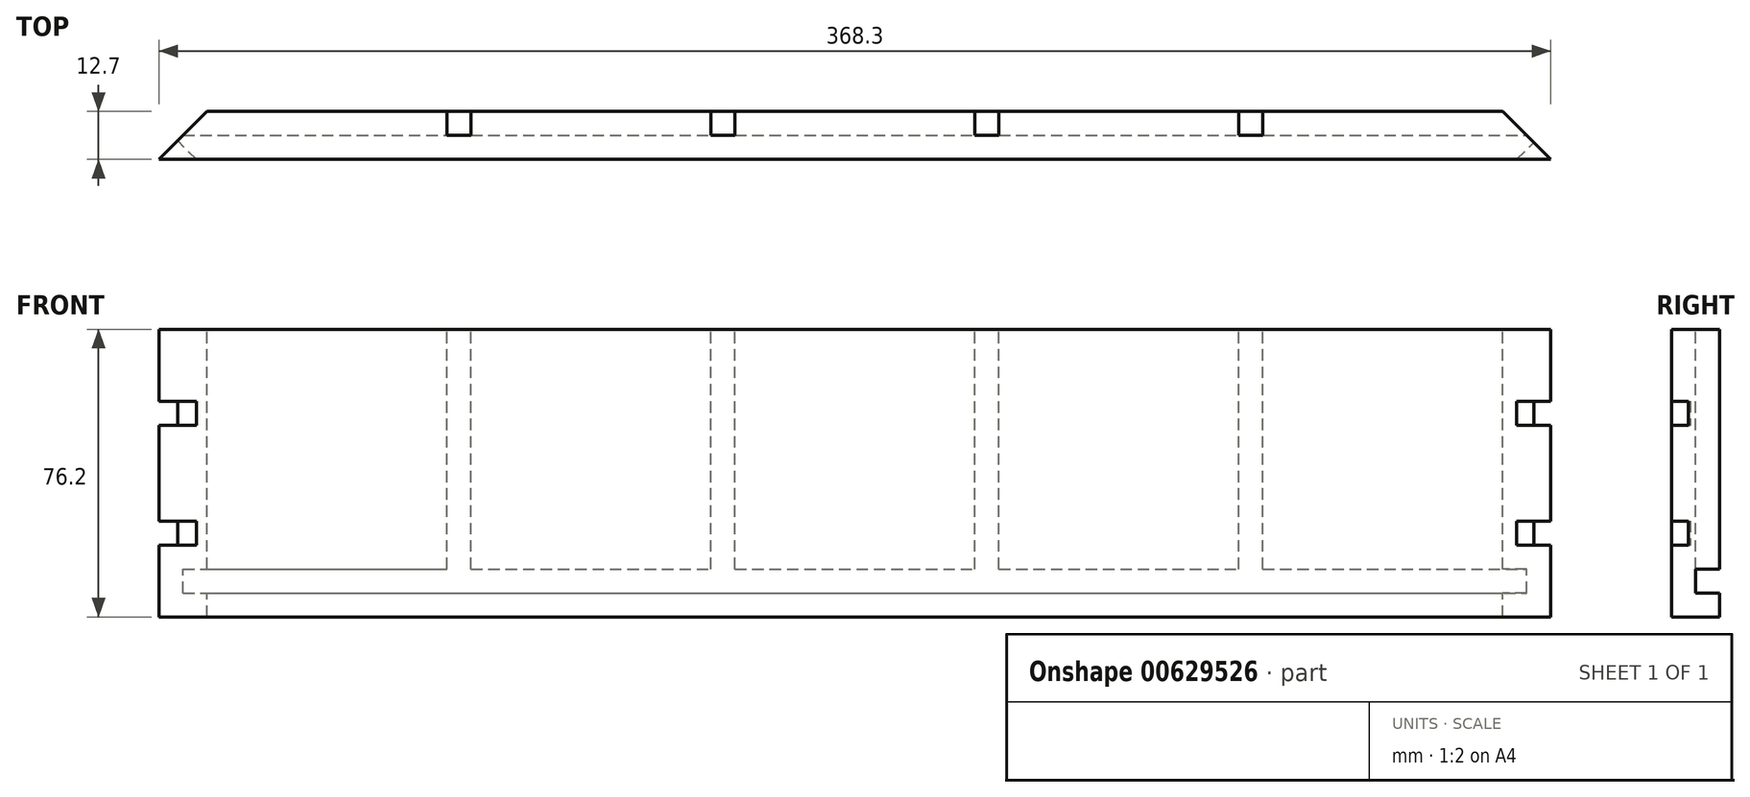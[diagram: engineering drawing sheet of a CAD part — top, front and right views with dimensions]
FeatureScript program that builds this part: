
annotation { "Feature Type Name" : "Feature", "Feature Type Description" : "" }
export const myFeature = defineFeature(function(context is Context, id is Id, definition is map)
    precondition{}
    {
        {
            var Q0;
            Q0=qCreatedBy(makeId("Front.planeOp"),FACE);
            var sketch = newSketch(context, id + "F0", { "sketchPlane" : qUnion([Q0])});
            skLineSegment(sketch, "E0.bottom", {"start": v(-184.15, 0) * mm, "end": v(184.15, 0) * mm});
            skLineSegment(sketch, "E0.top", {"start": v(-184.15, 76.2) * mm, "end": v(184.15, 76.2) * mm});
            skLineSegment(sketch, "E0.left", {"start": v(-184.15, 0) * mm, "end": v(-184.15, 76.2) * mm});
            skLineSegment(sketch, "E0.right", {"start": v(184.15, 0) * mm, "end": v(184.15, 76.2) * mm});
            skSolve(sketch);
        }
        {
            var Q0;
            Q0 = qSketchRegion(id + "F0", true);
            extrude(context, id + "F1", {"entities" : qUnion([Q0]), "depth" : 12.7 * mm, "offsetDistance" : 25.4 * mm});
        }
        {
            var Q0;
            Q0=makeQuery(id+"F1.opExtrude","SWEPT_FACE",FACE,{"disambiguationData":[OSD([sQuery(id+"F0.wireOp",EDGE,"E0.right")])]});
            var sketch = newSketch(context, id + "F2", { "sketchPlane" : qUnion([Q0])});
            skLineSegment(sketch, "E1.bottom", {"start": v(0, 12.7) * mm, "end": v(-6.35, 12.7) * mm});
            skLineSegment(sketch, "E1.top", {"start": v(0, 6.35) * mm, "end": v(-6.35, 6.35) * mm});
            skLineSegment(sketch, "E1.left", {"start": v(0, 12.7) * mm, "end": v(0, 6.35) * mm});
            skLineSegment(sketch, "E1.right", {"start": v(-6.35, 12.7) * mm, "end": v(-6.35, 6.35) * mm});
            skSolve(sketch);
        }
        {
            var Q0;
            Q0 = qSketchRegion(id + "F2", true);
            extrude(context, id + "F3", {"entities" : qUnion([Q0]), "operationType" : NewBodyOperationType.REMOVE, "endBound" : BoundingType.THROUGH_ALL, "oppositeDirection" : true, "depth" : 25.4 * mm, "offsetDistance" : 25.4 * mm});
        }
        {
            var Q0;
            Q0=makeQuery(id+"F1.opExtrude","SWEPT_FACE",FACE,{"disambiguationData":[OSD([sQuery(id+"F0.wireOp",EDGE,"E0.top")])]});
            var sketch = newSketch(context, id + "F4", { "sketchPlane" : qUnion([Q0])});
            skLineSegment(sketch, "E2", {"start": v(-184.15, -12.7) * mm, "end": v(-171.45, 0) * mm});
            skLineSegment(sketch, "E3", {"start": v(-171.45, 0) * mm, "end": v(-184.15, 0) * mm});
            skLineSegment(sketch, "E4", {"start": v(-184.15, 0) * mm, "end": v(-184.15, -12.7) * mm});
            skLineSegment(sketch, "E5.MirrorCS", {"start": v(184.15, 0) * mm, "end": v(184.15, -12.7) * mm});
            skLineSegment(sketch, "E6.MirrorCS", {"start": v(171.45, 0) * mm, "end": v(184.15, 0) * mm});
            skLineSegment(sketch, "E7.MirrorCS", {"start": v(184.15, -12.7) * mm, "end": v(171.45, 0) * mm});
            skSolve(sketch);
        }
        {
            var Q0;
            Q0 = qSketchRegion(id + "F4", true);
            extrude(context, id + "F5", {"entities" : qUnion([Q0]), "operationType" : NewBodyOperationType.REMOVE, "endBound" : BoundingType.THROUGH_ALL, "oppositeDirection" : true, "depth" : 25.4 * mm, "offsetDistance" : 25.4 * mm});
        }
        {
            var Q0;
            {var subQ0=sQuery(id+"F0.wireOp",EDGE,"E0.top");var subQ1=sQuery(id+"F0.wireOp",EDGE,"E0.left");var subQ2=sQuery(id+"F0.wireOp",EDGE,"E0.right");Q0=makeQuery(id+"F3.boolean.opBoolean","SPLIT",FACE,{"disambiguationData":[TD([makeQuery(id+"F1.opExtrude","SWEPT_FACE",FACE,{"disambiguationData":[OSD([subQ0])]})])],"derivedFrom":makeQuery(id+"F1.opExtrude","CAP_FACE",FACE,{"disambiguationData":[OSD([sQuery(id+"F0.wireOp",EDGE,"E0.bottom"),subQ0,subQ1,subQ2])],"isStart":true})});}
            var sketch = newSketch(context, id + "F6", { "sketchPlane" : qUnion([Q0])});
            skLineSegment(sketch, "E8.bottom", {"start": v(-107.95, 12.7) * mm, "end": v(-101.6, 12.7) * mm});
            skLineSegment(sketch, "E8.top", {"start": v(-107.95, 76.2) * mm, "end": v(-101.6, 76.2) * mm});
            skLineSegment(sketch, "E8.left", {"start": v(-101.6, 12.7) * mm, "end": v(-101.6, 76.2) * mm});
            skLineSegment(sketch, "E8.right", {"start": v(-107.95, 12.7) * mm, "end": v(-107.95, 76.2) * mm});
            skLineSegment(sketch, "E9.1.0.0", {"start": v(-38.1, 76.2) * mm, "end": v(-31.75, 76.2) * mm});
            skLineSegment(sketch, "E9.1.0.1", {"start": v(-31.75, 12.7) * mm, "end": v(-31.75, 76.2) * mm});
            skLineSegment(sketch, "E9.1.0.2", {"start": v(-38.1, 12.7) * mm, "end": v(-31.75, 12.7) * mm});
            skLineSegment(sketch, "E9.1.0.3", {"start": v(-38.1, 12.7) * mm, "end": v(-38.1, 76.2) * mm});
            skLineSegment(sketch, "E9.2.0.0", {"start": v(31.75, 76.2) * mm, "end": v(38.1, 76.2) * mm});
            skLineSegment(sketch, "E9.2.0.1", {"start": v(38.1, 12.7) * mm, "end": v(38.1, 76.2) * mm});
            skLineSegment(sketch, "E9.2.0.2", {"start": v(31.75, 12.7) * mm, "end": v(38.1, 12.7) * mm});
            skLineSegment(sketch, "E9.2.0.3", {"start": v(31.75, 12.7) * mm, "end": v(31.75, 76.2) * mm});
            skLineSegment(sketch, "E9.3.0.0", {"start": v(101.6, 76.2) * mm, "end": v(107.95, 76.2) * mm});
            skLineSegment(sketch, "E9.3.0.1", {"start": v(107.95, 12.7) * mm, "end": v(107.95, 76.2) * mm});
            skLineSegment(sketch, "E9.3.0.2", {"start": v(101.6, 12.7) * mm, "end": v(107.95, 12.7) * mm});
            skLineSegment(sketch, "E9.3.0.3", {"start": v(101.6, 12.7) * mm, "end": v(101.6, 76.2) * mm});
            skLineSegment(sketch, "E9.direction1", {"start": v(-107.95, 12.7) * mm, "end": v(-38.1, 12.7) * mm, "construction": true});
            skSolve(sketch);
        }
        {
            var Q0;
            Q0 = qSketchRegion(id + "F6", true);
            extrude(context, id + "F7", {"entities" : qUnion([Q0]), "operationType" : NewBodyOperationType.REMOVE, "oppositeDirection" : true, "depth" : 6.35 * mm, "offsetDistance" : 25.4 * mm});
        }
        {
            var Q0;
            Q0=makeQuery(id+"F5.boolean.opBoolean","COPY",FACE,{"derivedFrom":makeQuery(id+"F5.opExtrude","SWEPT_FACE",FACE,{"disambiguationData":[OSD([sQuery(id+"F4.wireOp",EDGE,"E2")])]})});
            var sketch = newSketch(context, id + "F8", { "sketchPlane" : qUnion([Q0])});
            skLineSegment(sketch, "E10.bottom", {"start": v(139.2, 57.15) * mm, "end": v(132.2, 57.15) * mm});
            skLineSegment(sketch, "E10.top", {"start": v(139.2, 50.8) * mm, "end": v(132.2, 50.8) * mm});
            skLineSegment(sketch, "E10.left", {"start": v(139.2, 57.15) * mm, "end": v(139.2, 50.8) * mm});
            skLineSegment(sketch, "E10.right", {"start": v(132.2, 57.15) * mm, "end": v(132.2, 50.8) * mm});
            skLineSegment(sketch, "E11.bottom", {"start": v(139.2, 25.4) * mm, "end": v(132.2, 25.4) * mm});
            skLineSegment(sketch, "E11.top", {"start": v(139.2, 19.05) * mm, "end": v(132.2, 19.05) * mm});
            skLineSegment(sketch, "E11.left", {"start": v(139.2, 25.4) * mm, "end": v(139.2, 19.05) * mm});
            skLineSegment(sketch, "E11.right", {"start": v(132.2, 25.4) * mm, "end": v(132.2, 19.05) * mm});
            skSolve(sketch);
        }
        {
            var Q0;
            Q0 = qSketchRegion(id + "F8", true);
            extrude(context, id + "F9", {"entities" : qUnion([Q0]), "operationType" : NewBodyOperationType.REMOVE, "endBound" : BoundingType.THROUGH_ALL, "oppositeDirection" : true, "depth" : 25.4 * mm, "offsetDistance" : 25.4 * mm});
        }
        {
            var Q0;
            Q0=makeQuery(id+"F5.boolean.opBoolean","COPY",FACE,{"derivedFrom":makeQuery(id+"F5.opExtrude","SWEPT_FACE",FACE,{"disambiguationData":[OSD([sQuery(id+"F4.wireOp",EDGE,"E7.MirrorCS")])]})});
            var sketch = newSketch(context, id + "F10", { "sketchPlane" : qUnion([Q0])});
            skLineSegment(sketch, "E12.bottom", {"start": v(-139.2, 57.15) * mm, "end": v(-132.84, 57.15) * mm});
            skLineSegment(sketch, "E12.top", {"start": v(-139.2, 50.8) * mm, "end": v(-132.84, 50.8) * mm});
            skLineSegment(sketch, "E12.left", {"start": v(-139.2, 57.15) * mm, "end": v(-139.2, 50.8) * mm});
            skLineSegment(sketch, "E12.right", {"start": v(-132.84, 57.15) * mm, "end": v(-132.84, 50.8) * mm});
            skLineSegment(sketch, "E13.bottom", {"start": v(-139.2, 25.4) * mm, "end": v(-132.84, 25.4) * mm});
            skLineSegment(sketch, "E13.top", {"start": v(-139.2, 19.05) * mm, "end": v(-132.84, 19.05) * mm});
            skLineSegment(sketch, "E13.left", {"start": v(-139.2, 25.4) * mm, "end": v(-139.2, 19.05) * mm});
            skLineSegment(sketch, "E13.right", {"start": v(-132.84, 25.4) * mm, "end": v(-132.84, 19.05) * mm});
            skSolve(sketch);
        }
        {
            var Q0;
            Q0 = qSketchRegion(id + "F10", true);
            extrude(context, id + "F11", {"entities" : qUnion([Q0]), "operationType" : NewBodyOperationType.REMOVE, "endBound" : BoundingType.THROUGH_ALL, "oppositeDirection" : true, "depth" : 25.4 * mm, "offsetDistance" : 25.4 * mm});
        }
    });
